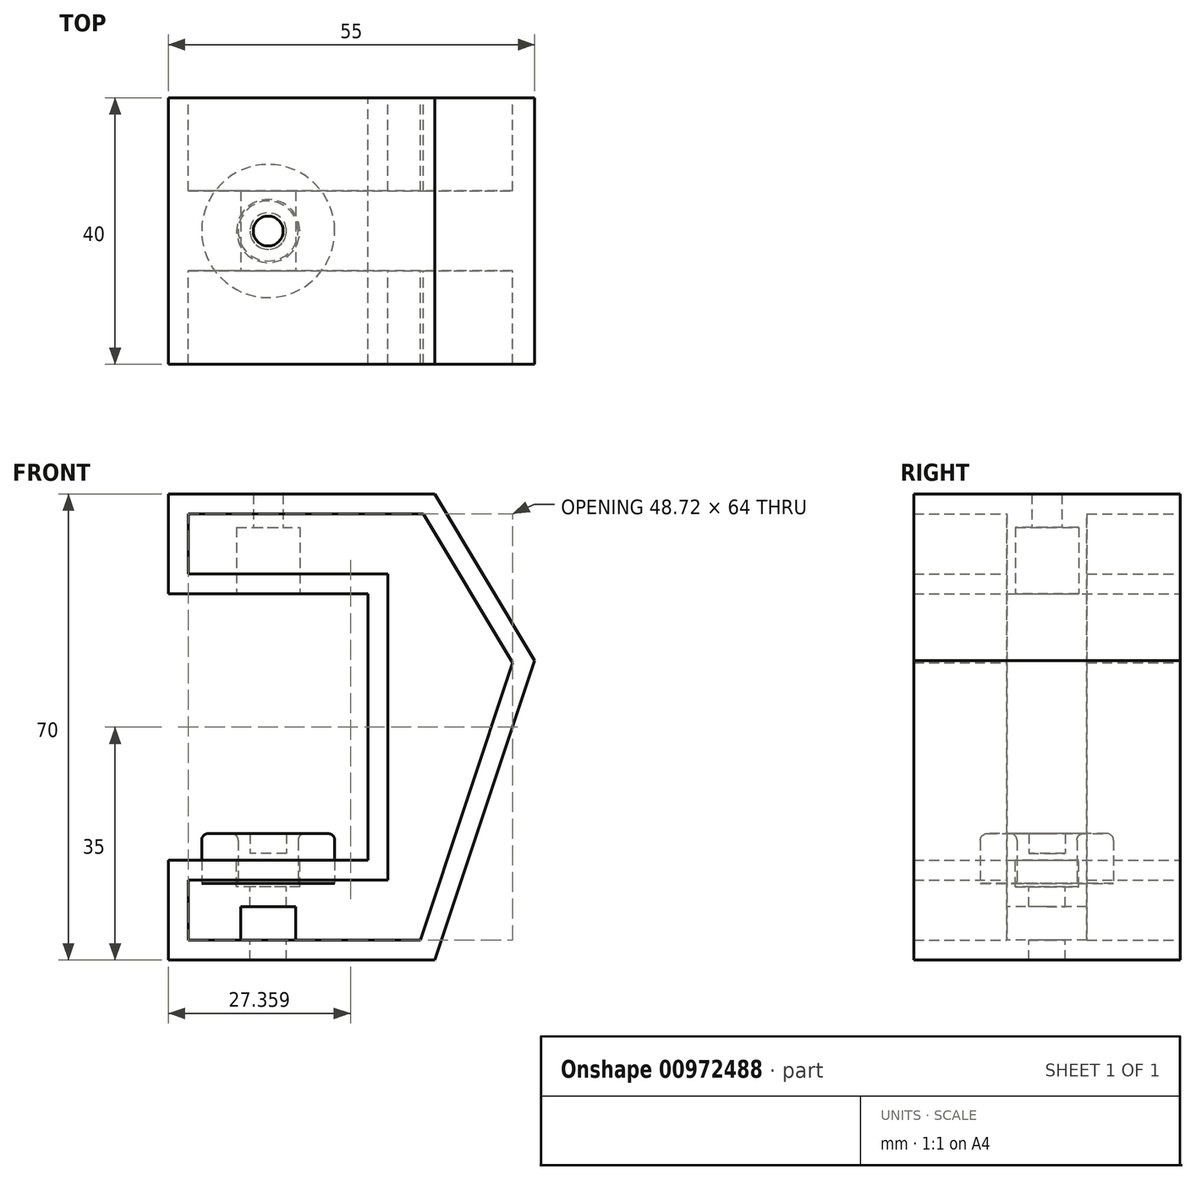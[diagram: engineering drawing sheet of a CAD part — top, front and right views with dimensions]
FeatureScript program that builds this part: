
annotation { "Feature Type Name" : "Feature", "Feature Type Description" : "" }
export const myFeature = defineFeature(function(context is Context, id is Id, definition is map)
    precondition{}
    {
        {
            var Q0;
            Q0=qCreatedBy(makeId("Front.planeOp"),FACE);
            var sketch = newSketch(context, id + "F0", { "sketchPlane" : qUnion([Q0])});
            skLineSegment(sketch, "E0", {"start": v(0, 21.86) * mm, "end": v(-30, 21.86) * mm});
            skLineSegment(sketch, "E1", {"start": v(-30, 21.86) * mm, "end": v(-30, 36.86) * mm});
            skLineSegment(sketch, "E2", {"start": v(-30, 36.86) * mm, "end": v(10, 36.86) * mm});
            skLineSegment(sketch, "E3", {"start": v(0, -33.14) * mm, "end": v(-30, -33.14) * mm});
            skLineSegment(sketch, "E4", {"start": v(-30, -33.14) * mm, "end": v(-30, -18.14) * mm});
            skLineSegment(sketch, "E5", {"start": v(-30, -18.14) * mm, "end": v(0, -18.14) * mm});
            skLineSegment(sketch, "E6", {"start": v(0, -18.14) * mm, "end": v(0, 21.86) * mm});
            skLineSegment(sketch, "E7", {"start": v(10, -33.14) * mm, "end": v(0, -33.14) * mm});
            skLineSegment(sketch, "E8", {"start": v(10, 36.86) * mm, "end": v(25, 11.86) * mm});
            skLineSegment(sketch, "E9", {"start": v(25, 11.86) * mm, "end": v(10, -33.14) * mm});
            skPoint(sketch, "E10", {"position": v(-15, 21.86) * mm});
            skPoint(sketch, "E11", {"position": v(-15, -18.14) * mm});
            skLineSegment(sketch, "E12", {"start": v(0, 21.86) * mm, "end": v(0, 36.86) * mm});
            skLineSegment(sketch, "E13", {"start": v(0, -18.14) * mm, "end": v(0, -33.14) * mm});
            skLineSegment(sketch, "E14", {"start": v(-30, -18.14) * mm, "end": v(10, -33.14) * mm});
            skLineSegment(sketch, "E15", {"start": v(10, -33.14) * mm, "end": v(0, -18.14) * mm});
            skLineSegment(sketch, "E16", {"start": v(25, 11.86) * mm, "end": v(0, -18.14) * mm});
            skLineSegment(sketch, "E17", {"start": v(10, 36.86) * mm, "end": v(0, 21.86) * mm});
            skLineSegment(sketch, "E18", {"start": v(25, 11.86) * mm, "end": v(0, 21.86) * mm});
            skLineSegment(sketch, "E19", {"start": v(10, 36.86) * mm, "end": v(-30, 21.86) * mm});
            skLineSegment(sketch, "E20", {"start": v(-30, 36.86) * mm, "end": v(0, 21.86) * mm});
            skLineSegment(sketch, "E21", {"start": v(-30, -33.14) * mm, "end": v(0, -18.14) * mm});
            skSolve(sketch);
        }
        {
            var Q0;
            Q0=qSketchRegion(id+"F0",true);
            extrude(context, id + "F1", {"entities" : qUnion([Q0]), "depth" : 20 * mm, "offsetDistance" : 25 * mm, "hasSecondDirection" : true, "secondDirectionOppositeDirection" : true, "secondDirectionDepth" : 20 * mm});
        }
        {
            var Q0;
            Q0=makeQuery(id+"F1.opExtrude","CAP_FACE",FACE,{"disambiguationData":[OSD([sQuery(id+"F0.wireOp",EDGE,"E0"),sQuery(id+"F0.wireOp",EDGE,"E1"),sQuery(id+"F0.wireOp",EDGE,"E2"),sQuery(id+"F0.wireOp",EDGE,"E3"),sQuery(id+"F0.wireOp",EDGE,"E4"),sQuery(id+"F0.wireOp",EDGE,"E5"),sQuery(id+"F0.wireOp",EDGE,"E6"),sQuery(id+"F0.wireOp",EDGE,"E7"),sQuery(id+"F0.wireOp",EDGE,"E8"),sQuery(id+"F0.wireOp",EDGE,"E9")])],"isStart":false});
            var Q1;
            Q1=makeQuery(id+"F1.opExtrude","CAP_FACE",FACE,{"disambiguationData":[OSD([sQuery(id+"F0.wireOp",EDGE,"E0"),sQuery(id+"F0.wireOp",EDGE,"E1"),sQuery(id+"F0.wireOp",EDGE,"E2"),sQuery(id+"F0.wireOp",EDGE,"E3"),sQuery(id+"F0.wireOp",EDGE,"E4"),sQuery(id+"F0.wireOp",EDGE,"E5"),sQuery(id+"F0.wireOp",EDGE,"E6"),sQuery(id+"F0.wireOp",EDGE,"E7"),sQuery(id+"F0.wireOp",EDGE,"E8"),sQuery(id+"F0.wireOp",EDGE,"E9")])],"isStart":true});
            shell(context, id + "F2", {"entities" : qUnion([Q0, Q1]), "thickness" : 3 * mm});
        }
        {
            var Q0;
            Q0=qSketchRegion(id+"F0",true);
            extrude(context, id + "F3", {"entities" : qUnion([Q0]), "operationType" : NewBodyOperationType.ADD, "depth" : 6 * mm, "offsetDistance" : 25 * mm, "hasSecondDirection" : true, "secondDirectionOppositeDirection" : true, "secondDirectionDepth" : 6 * mm});
        }
        {
            var Q0;
            Q0=makeQuery(id+"F3.opExtrude","CAP_FACE",FACE,{"disambiguationData":[OSD([sQuery(id+"F0.wireOp",EDGE,"E0"),sQuery(id+"F0.wireOp",EDGE,"E1"),sQuery(id+"F0.wireOp",EDGE,"E2"),sQuery(id+"F0.wireOp",EDGE,"E3"),sQuery(id+"F0.wireOp",EDGE,"E4"),sQuery(id+"F0.wireOp",EDGE,"E5"),sQuery(id+"F0.wireOp",EDGE,"E6"),sQuery(id+"F0.wireOp",EDGE,"E7"),sQuery(id+"F0.wireOp",EDGE,"E8"),sQuery(id+"F0.wireOp",EDGE,"E9")])],"isStart":false});
            var sketch = newSketch(context, id + "F4", { "sketchPlane" : qUnion([Q0])});
            skLineSegment(sketch, "E22.bottom", {"start": v(-27, -21.14) * mm, "end": v(7.84, -21.14) * mm});
            skLineSegment(sketch, "E22.top", {"start": v(-27, -30.14) * mm, "end": v(7.84, -30.14) * mm});
            skLineSegment(sketch, "E22.left", {"start": v(-27, -21.14) * mm, "end": v(-27, -30.14) * mm});
            skLineSegment(sketch, "E22.right", {"start": v(7.84, -21.14) * mm, "end": v(7.84, -30.14) * mm});
            skLineSegment(sketch, "E23", {"start": v(-15, -30.14) * mm, "end": v(-15, -21.14) * mm});
            skLineSegment(sketch, "E24", {"start": v(-19.15, -25.14) * mm, "end": v(-10.85, -25.14) * mm});
            skLineSegment(sketch, "E25", {"start": v(-19.15, -25.14) * mm, "end": v(-19.15, -30.14) * mm});
            skLineSegment(sketch, "E26", {"start": v(-10.85, -25.14) * mm, "end": v(-10.85, -30.14) * mm});
            skLineSegment(sketch, "E27", {"start": v(-19.15, -30.14) * mm, "end": v(-25.5, -21.14) * mm});
            skLineSegment(sketch, "E28", {"start": v(-21.15, -30.14) * mm, "end": v(-27, -21.85) * mm});
            skLineSegment(sketch, "E29", {"start": v(-27, -21.85) * mm, "end": v(-27, -21.14) * mm});
            skLineSegment(sketch, "E30", {"start": v(-21.15, -30.14) * mm, "end": v(-19.15, -30.14) * mm});
            skLineSegment(sketch, "E31", {"start": v(-10.85, -30.14) * mm, "end": v(3, -21.14) * mm});
            skLineSegment(sketch, "E32", {"start": v(-22.32, -25.64) * mm, "end": v(-15, -21.14) * mm});
            skLineSegment(sketch, "E33", {"start": v(-21.75, -26.46) * mm, "end": v(-13.1, -21.14) * mm});
            skPoint(sketch, "E34", {"position": v(-8.85, -30.14) * mm});
            skLineSegment(sketch, "E35", {"start": v(-8.85, -30.14) * mm, "end": v(12.45, -16.3) * mm});
            skPoint(sketch, "E36", {"position": v(-16.9, -21.14) * mm});
            skLineSegment(sketch, "E37.MirrorCS", {"start": v(-7.68, -25.64) * mm, "end": v(-15, -21.14) * mm});
            skLineSegment(sketch, "E38", {"start": v(-16.9, -21.14) * mm, "end": v(-6.67, -27.43) * mm});
            skLineSegment(sketch, "E39", {"start": v(-15, -21.14) * mm, "end": v(-5.75, -26.82) * mm});
            skLineSegment(sketch, "E40.bottom", {"start": v(3, -21.14) * mm, "end": v(8.3, -21.14) * mm});
            skLineSegment(sketch, "E40.top", {"start": v(3, 33.86) * mm, "end": v(8.3, 33.86) * mm});
            skLineSegment(sketch, "E40.left", {"start": v(3, -21.14) * mm, "end": v(3, 33.86) * mm});
            skLineSegment(sketch, "E40.right", {"start": v(8.3, -21.14) * mm, "end": v(8.3, 33.86) * mm});
            skLineSegment(sketch, "E41.bottom", {"start": v(-27, 33.86) * mm, "end": v(3, 33.86) * mm});
            skLineSegment(sketch, "E41.top", {"start": v(-27, 24.86) * mm, "end": v(3, 24.86) * mm});
            skLineSegment(sketch, "E41.left", {"start": v(-27, 33.86) * mm, "end": v(-27, 24.86) * mm});
            skLineSegment(sketch, "E41.right", {"start": v(3, 33.86) * mm, "end": v(3, 24.86) * mm});
            skLineSegment(sketch, "E42.bottom", {"start": v(8.3, 33.86) * mm, "end": v(21.72, 33.86) * mm});
            skLineSegment(sketch, "E42.top", {"start": v(8.3, 11.5) * mm, "end": v(21.72, 11.5) * mm});
            skLineSegment(sketch, "E42.left", {"start": v(8.3, 33.86) * mm, "end": v(8.3, 11.5) * mm});
            skLineSegment(sketch, "E42.right", {"start": v(21.72, 33.86) * mm, "end": v(21.72, 11.5) * mm});
            skLineSegment(sketch, "E43.bottom", {"start": v(7.84, -30.14) * mm, "end": v(21.72, -30.14) * mm});
            skLineSegment(sketch, "E43.top", {"start": v(7.84, 11.5) * mm, "end": v(21.72, 11.5) * mm});
            skLineSegment(sketch, "E43.left", {"start": v(7.84, -30.14) * mm, "end": v(7.84, 11.5) * mm});
            skLineSegment(sketch, "E43.right", {"start": v(21.72, -30.14) * mm, "end": v(21.72, 11.5) * mm});
            skLineSegment(sketch, "E44", {"start": v(3, -21.14) * mm, "end": v(13, -14.64) * mm});
            skLineSegment(sketch, "E45", {"start": v(3, 6.36) * mm, "end": v(15, 22.68) * mm});
            skLineSegment(sketch, "E46", {"start": v(3, 6.36) * mm, "end": v(14.78, -9.32) * mm});
            skLineSegment(sketch, "E47", {"start": v(3, 9.1) * mm, "end": v(15.41, -7.42) * mm});
            skLineSegment(sketch, "E48", {"start": v(3, 3.25) * mm, "end": v(16.04, 20.96) * mm});
            skLineSegment(sketch, "E49", {"start": v(21.72, 11.5) * mm, "end": v(3, -21.14) * mm});
            skLineSegment(sketch, "E50", {"start": v(3, -21.14) * mm, "end": v(7.84, -30.14) * mm});
            skLineSegment(sketch, "E51", {"start": v(5.76, -19.35) * mm, "end": v(19.32, 4.3) * mm});
            skLineSegment(sketch, "E52", {"start": v(3, -18.13) * mm, "end": v(20.83, 12.97) * mm});
            skLineSegment(sketch, "E53", {"start": v(5.89, -8.16) * mm, "end": v(12.43, -11.91) * mm});
            skPoint(sketch, "E54", {"position": v(9.32, -10.13) * mm});
            skPoint(sketch, "E55", {"position": v(10.62, -10.87) * mm});
            skPoint(sketch, "E56", {"position": v(8.01, -9.38) * mm});
            skPoint(sketch, "E57", {"position": v(5.2, -25.23) * mm});
            skPoint(sketch, "E58", {"position": v(3.87, -25.93) * mm});
            skLineSegment(sketch, "E59", {"start": v(3.87, -25.93) * mm, "end": v(7.4, -24.03) * mm});
            skPoint(sketch, "E60", {"position": v(6.51, -24.5) * mm});
            skLineSegment(sketch, "E61", {"start": v(3.87, -25.93) * mm, "end": v(1.3, -21.14) * mm});
            skPoint(sketch, "E62", {"position": v(1.3, -21.14) * mm});
            skLineSegment(sketch, "E63", {"start": v(6.51, -24.5) * mm, "end": v(4.78, -21.28) * mm});
            skLineSegment(sketch, "E64", {"start": v(3.87, -25.93) * mm, "end": v(6.13, -30.14) * mm});
            skLineSegment(sketch, "E65", {"start": v(6.51, -24.5) * mm, "end": v(8.49, -28.19) * mm});
            skLineSegment(sketch, "E66", {"start": v(21.72, 11.5) * mm, "end": v(3, 24.86) * mm});
            skLineSegment(sketch, "E67", {"start": v(3, 24.86) * mm, "end": v(-12, 33.86) * mm});
            skLineSegment(sketch, "E68", {"start": v(3, 24.86) * mm, "end": v(4.16, 26.49) * mm});
            skLineSegment(sketch, "E69", {"start": v(4.16, 26.49) * mm, "end": v(-8.12, 33.86) * mm});
            skLineSegment(sketch, "E70", {"start": v(4.16, 26.49) * mm, "end": v(19.14, 15.8) * mm});
            skLineSegment(sketch, "E71", {"start": v(8.3, 33.86) * mm, "end": v(3, 24.86) * mm});
            skLineSegment(sketch, "E72", {"start": v(5.65, 29.36) * mm, "end": v(4.36, 30.12) * mm});
            skLineSegment(sketch, "E73", {"start": v(5.65, 29.36) * mm, "end": v(6.94, 28.6) * mm});
            skLineSegment(sketch, "E74", {"start": v(4.36, 30.12) * mm, "end": v(6.56, 33.86) * mm});
            skLineSegment(sketch, "E75", {"start": v(6.94, 28.6) * mm, "end": v(3, 21.9) * mm});
            skLineSegment(sketch, "E76", {"start": v(6.94, 28.6) * mm, "end": v(9.18, 32.4) * mm});
            skLineSegment(sketch, "E77", {"start": v(4.36, 30.12) * mm, "end": v(1.2, 24.86) * mm});
            skSolve(sketch);
        }
        {
            var Q0;
            {var subQ3=sQuery(id+"F4.wireOp",EDGE,"E25");Q0=makeQuery(id+"F4.imprint","IMPRINT",FACE,{"disambiguationData":[TD([[makeQuery(id+"F4.imprint","IMPRINT",EDGE,{"derivedFrom":subQ3}),1.0]])]});}
            var Q1;
            {var subQ3=sQuery(id+"F4.wireOp",EDGE,"E26");Q1=makeQuery(id+"F4.imprint","IMPRINT",FACE,{"disambiguationData":[TD([[makeQuery(id+"F4.imprint","IMPRINT",EDGE,{"derivedFrom":subQ3}),-1.0]])]});}
            extrude(context, id + "F5", {"entities" : qUnion([Q0, Q1]), "operationType" : NewBodyOperationType.REMOVE, "oppositeDirection" : true, "depth" : 15 * mm, "offsetDistance" : 25 * mm});
        }
        {
            var Q0;
            Q0=makeQuery(id+"F1.opExtrude","SWEPT_FACE",FACE,{"disambiguationData":[OSD([sQuery(id+"F0.wireOp",EDGE,"E0")])]});
            var sketch = newSketch(context, id + "F6", { "sketchPlane" : qUnion([Q0])});
            skLineSegment(sketch, "E78.bottom", {"start": v(-30, -20) * mm, "end": v(0, -20) * mm});
            skLineSegment(sketch, "E78.top", {"start": v(-30, 20) * mm, "end": v(0, 20) * mm});
            skLineSegment(sketch, "E78.left", {"start": v(-30, -20) * mm, "end": v(-30, 20) * mm});
            skLineSegment(sketch, "E78.right", {"start": v(0, -20) * mm, "end": v(0, 20) * mm});
            skLineSegment(sketch, "E79", {"start": v(-30, 0) * mm, "end": v(0, 0) * mm});
            skLineSegment(sketch, "E80", {"start": v(-15, 20) * mm, "end": v(-15, -20) * mm});
            skPoint(sketch, "E81", {"position": v(-15, 0) * mm});
            skSolve(sketch);
        }
        {
            var Q0;
            Q0=sQuery(id+"F6.wireOp",VERTEX,"E81");
            var Q1;
            Q1=makeQuery(id+"F1.opExtrude","SWEPT_BODY",BODY,{"disambiguationData":[OSD([sQuery(id+"F0.wireOp",EDGE,"E0"),sQuery(id+"F0.wireOp",EDGE,"E1"),sQuery(id+"F0.wireOp",EDGE,"E2"),sQuery(id+"F0.wireOp",EDGE,"E3"),sQuery(id+"F0.wireOp",EDGE,"E4"),sQuery(id+"F0.wireOp",EDGE,"E5"),sQuery(id+"F0.wireOp",EDGE,"E6"),sQuery(id+"F0.wireOp",EDGE,"E7"),sQuery(id+"F0.wireOp",EDGE,"E8"),sQuery(id+"F0.wireOp",EDGE,"E9")])]});
            hole(context, id + "F7", {"style" : HoleStyle.C_BORE, "endStyle" : HoleEndStyle.BLIND, "holeDiameter" : 4.5 * mm, "cBoreDiameter" : 9.5 * mm, "cBoreDepth" : 10 * mm, "majorDiameter" : 5 * mm, "holeDepth" : 20 * mm, "isTappedThrough" : true, "tappedDepth" : 12 * mm, "tapClearance" : 3, "startFromSketch" : true, "locations" : qUnion([Q0]), "scope" : qUnion([Q1])});
        }
        {
            var Q0;
            Q0=makeQuery(id+"F1.opExtrude","SWEPT_FACE",FACE,{"disambiguationData":[OSD([sQuery(id+"F0.wireOp",EDGE,"E5")])]});
            var sketch = newSketch(context, id + "F8", { "sketchPlane" : qUnion([Q0])});
            skLineSegment(sketch, "E82.bottom", {"start": v(0, -20) * mm, "end": v(-30, -20) * mm});
            skLineSegment(sketch, "E82.top", {"start": v(0, 20) * mm, "end": v(-30, 20) * mm});
            skLineSegment(sketch, "E82.left", {"start": v(0, -20) * mm, "end": v(0, 20) * mm});
            skLineSegment(sketch, "E82.right", {"start": v(-30, -20) * mm, "end": v(-30, 20) * mm});
            skLineSegment(sketch, "E83", {"start": v(-15, -20) * mm, "end": v(-15, 20) * mm});
            skPoint(sketch, "E84", {"position": v(-15, 0) * mm});
            skCircle(sketch, "E85", {"center": v(-15, 0) * mm, "radius": 2.75 * mm});
            skCircle(sketch, "E86", {"center": v(-15, 0) * mm, "radius": 4.5 * mm});
            skCircle(sketch, "E87", {"center": v(-15, 0) * mm, "radius": 10 * mm});
            skSolve(sketch);
        }
        {
            var Q0;
            Q0=sQuery(id+"F8.wireOp",VERTEX,"E84");
            var Q1;
            Q1=makeQuery(id+"F1.opExtrude","SWEPT_BODY",BODY,{"disambiguationData":[OSD([sQuery(id+"F0.wireOp",EDGE,"E0"),sQuery(id+"F0.wireOp",EDGE,"E1"),sQuery(id+"F0.wireOp",EDGE,"E2"),sQuery(id+"F0.wireOp",EDGE,"E3"),sQuery(id+"F0.wireOp",EDGE,"E4"),sQuery(id+"F0.wireOp",EDGE,"E5"),sQuery(id+"F0.wireOp",EDGE,"E6"),sQuery(id+"F0.wireOp",EDGE,"E7"),sQuery(id+"F0.wireOp",EDGE,"E8"),sQuery(id+"F0.wireOp",EDGE,"E9")])]});
            hole(context, id + "F9", {"style" : HoleStyle.C_BORE, "endStyle" : HoleEndStyle.BLIND, "holeDiameter" : 5.5 * mm, "cBoreDiameter" : 9.5 * mm, "cBoreDepth" : 4 * mm, "majorDiameter" : 5 * mm, "holeDepth" : 20 * mm, "isTappedThrough" : true, "tappedDepth" : 12 * mm, "tapClearance" : 3, "startFromSketch" : true, "locations" : qUnion([Q0]), "scope" : qUnion([Q1])});
        }
        {
            var Q0;
            {var subQ0=sQuery(id+"F8.wireOp",EDGE,"E86");var subQ1=sQuery(id+"F8.wireOp",EDGE,"E83");var subQ2=makeQuery(id+"F8.imprint","INTERSECT",VERTEX,{"disambiguationData":[OD(0.0)],"derivedFrom":[subQ1,subQ0]});Q0=makeQuery(id+"F8.imprint","IMPRINT",FACE,{"disambiguationData":[TD([[makeQuery(id+"F8.imprint","IMPRINT",EDGE,{"disambiguationData":[TD([[subQ2,-1.0]])],"derivedFrom":subQ1}),-1.0]])]});}
            var Q1;
            {var subQ0=sQuery(id+"F8.wireOp",EDGE,"E86");var subQ1=sQuery(id+"F8.wireOp",EDGE,"E83");var subQ2=makeQuery(id+"F8.imprint","INTERSECT",VERTEX,{"disambiguationData":[OD(0.0)],"derivedFrom":[subQ1,subQ0]});Q1=makeQuery(id+"F8.imprint","IMPRINT",FACE,{"disambiguationData":[TD([[makeQuery(id+"F8.imprint","IMPRINT",EDGE,{"disambiguationData":[TD([[subQ2,-1.0]])],"derivedFrom":subQ1}),1.0]])]});}
            extrude(context, id + "F10", {"entities" : qUnion([Q0, Q1]), "depth" : 1 * mm, "offsetDistance" : 25 * mm, "hasSecondDirection" : true, "secondDirectionOppositeDirection" : true, "secondDirectionDepth" : 3.5 * mm});
        }
        {
            var Q0;
            {var subQ0=sQuery(id+"F8.wireOp",EDGE,"E87");var subQ1=sQuery(id+"F8.wireOp",EDGE,"E83");var subQ2=makeQuery(id+"F8.imprint","INTERSECT",VERTEX,{"disambiguationData":[OD(0.0)],"derivedFrom":[subQ1,subQ0]});Q0=makeQuery(id+"F8.imprint","IMPRINT",FACE,{"disambiguationData":[TD([[makeQuery(id+"F8.imprint","IMPRINT",EDGE,{"disambiguationData":[TD([[subQ2,-1.0]])],"derivedFrom":subQ1}),-1.0]])]});}
            var Q1;
            {var subQ0=sQuery(id+"F8.wireOp",EDGE,"E87");var subQ1=sQuery(id+"F8.wireOp",EDGE,"E83");var subQ2=makeQuery(id+"F8.imprint","INTERSECT",VERTEX,{"disambiguationData":[OD(0.0)],"derivedFrom":[subQ1,subQ0]});Q1=makeQuery(id+"F8.imprint","IMPRINT",FACE,{"disambiguationData":[TD([[makeQuery(id+"F8.imprint","IMPRINT",EDGE,{"disambiguationData":[TD([[subQ2,-1.0]])],"derivedFrom":subQ1}),1.0]])]});}
            var Q2;
            {var subQ0=sQuery(id+"F8.wireOp",EDGE,"E86");var subQ1=sQuery(id+"F8.wireOp",EDGE,"E83");var subQ2=makeQuery(id+"F8.imprint","INTERSECT",VERTEX,{"disambiguationData":[OD(0.0)],"derivedFrom":[subQ1,subQ0]});Q2=makeQuery(id+"F8.imprint","IMPRINT",FACE,{"disambiguationData":[TD([[makeQuery(id+"F8.imprint","IMPRINT",EDGE,{"disambiguationData":[TD([[subQ2,-1.0]])],"derivedFrom":subQ1}),1.0]])]});}
            var Q3;
            {var subQ0=sQuery(id+"F8.wireOp",EDGE,"E86");var subQ1=sQuery(id+"F8.wireOp",EDGE,"E83");var subQ2=makeQuery(id+"F8.imprint","INTERSECT",VERTEX,{"disambiguationData":[OD(0.0)],"derivedFrom":[subQ1,subQ0]});Q3=makeQuery(id+"F8.imprint","IMPRINT",FACE,{"disambiguationData":[TD([[makeQuery(id+"F8.imprint","IMPRINT",EDGE,{"disambiguationData":[TD([[subQ2,-1.0]])],"derivedFrom":subQ1}),-1.0]])]});}
            var Q4;
            {var subQ0=sQuery(id+"F8.wireOp",EDGE,"E85");var subQ1=sQuery(id+"F8.wireOp",EDGE,"E83");var subQ2=makeQuery(id+"F8.imprint","INTERSECT",VERTEX,{"disambiguationData":[OD(0.0)],"derivedFrom":[subQ1,subQ0]});Q4=makeQuery(id+"F8.imprint","IMPRINT",FACE,{"disambiguationData":[TD([[makeQuery(id+"F8.imprint","IMPRINT",EDGE,{"disambiguationData":[TD([[subQ2,-1.0]])],"derivedFrom":subQ1}),-1.0]])]});}
            var Q5;
            {var subQ0=sQuery(id+"F8.wireOp",EDGE,"E85");var subQ1=sQuery(id+"F8.wireOp",EDGE,"E83");var subQ2=makeQuery(id+"F8.imprint","INTERSECT",VERTEX,{"disambiguationData":[OD(0.0)],"derivedFrom":[subQ1,subQ0]});Q5=makeQuery(id+"F8.imprint","IMPRINT",FACE,{"disambiguationData":[TD([[makeQuery(id+"F8.imprint","IMPRINT",EDGE,{"disambiguationData":[TD([[subQ2,-1.0]])],"derivedFrom":subQ1}),1.0]])]});}
            extrude(context, id + "F11", {"entities" : qUnion([Q0, Q1, Q2, Q3, Q4, Q5]), "operationType" : NewBodyOperationType.ADD, "depth" : 4 * mm, "offsetDistance" : 25 * mm, "hasSecondDirection" : true, "secondDirectionOppositeDirection" : false, "secondDirectionDepth" : 1 * mm});
        }
        {
            var Q0;
            Q0=makeQuery(id+"F11.opExtrude","CAP_FACE",FACE,{"disambiguationData":[OSD([sQuery(id+"F8.wireOp",EDGE,"E87")])],"isStart":false});
            var Q1;
            Q1=makeQuery(id+"F11.opExtrude","CAP_EDGE",EDGE,{"disambiguationData":[OSD([sQuery(id+"F8.wireOp",EDGE,"E87")])],"isStart":true});
            fillet(context, id + "F12", {"entities" : qUnion([Q0, Q1]), "radius" : 1 * mm, "tangentPropagation" : true, "allowEdgeOverflow" : false});
        }
        {
            var Q0;
            Q0=makeQuery(id+"F10.opExtrude","CAP_EDGE",EDGE,{"disambiguationData":[OSD([sQuery(id+"F8.wireOp",EDGE,"E86")])],"isStart":false});
            var Q1;
            Q1=makeQuery(id+"F10.opExtrude","CAP_EDGE",EDGE,{"disambiguationData":[OSD([sQuery(id+"F8.wireOp",EDGE,"E86")])],"isStart":true});
            var Q2;
            Q2=makeQuery(id+"F10.opExtrude","CAP_EDGE",EDGE,{"disambiguationData":[OSD([sQuery(id+"F8.wireOp",EDGE,"E85")])],"isStart":true});
            var Q3;
            Q3=makeQuery(id+"F10.opExtrude","CAP_EDGE",EDGE,{"disambiguationData":[OSD([sQuery(id+"F8.wireOp",EDGE,"E85")])],"isStart":false});
            fillet(context, id + "F13", {"entities" : qUnion([Q0, Q1, Q2, Q3]), "radius" : 0.5 * mm, "tangentPropagation" : true, "allowEdgeOverflow" : false});
        }
    });
